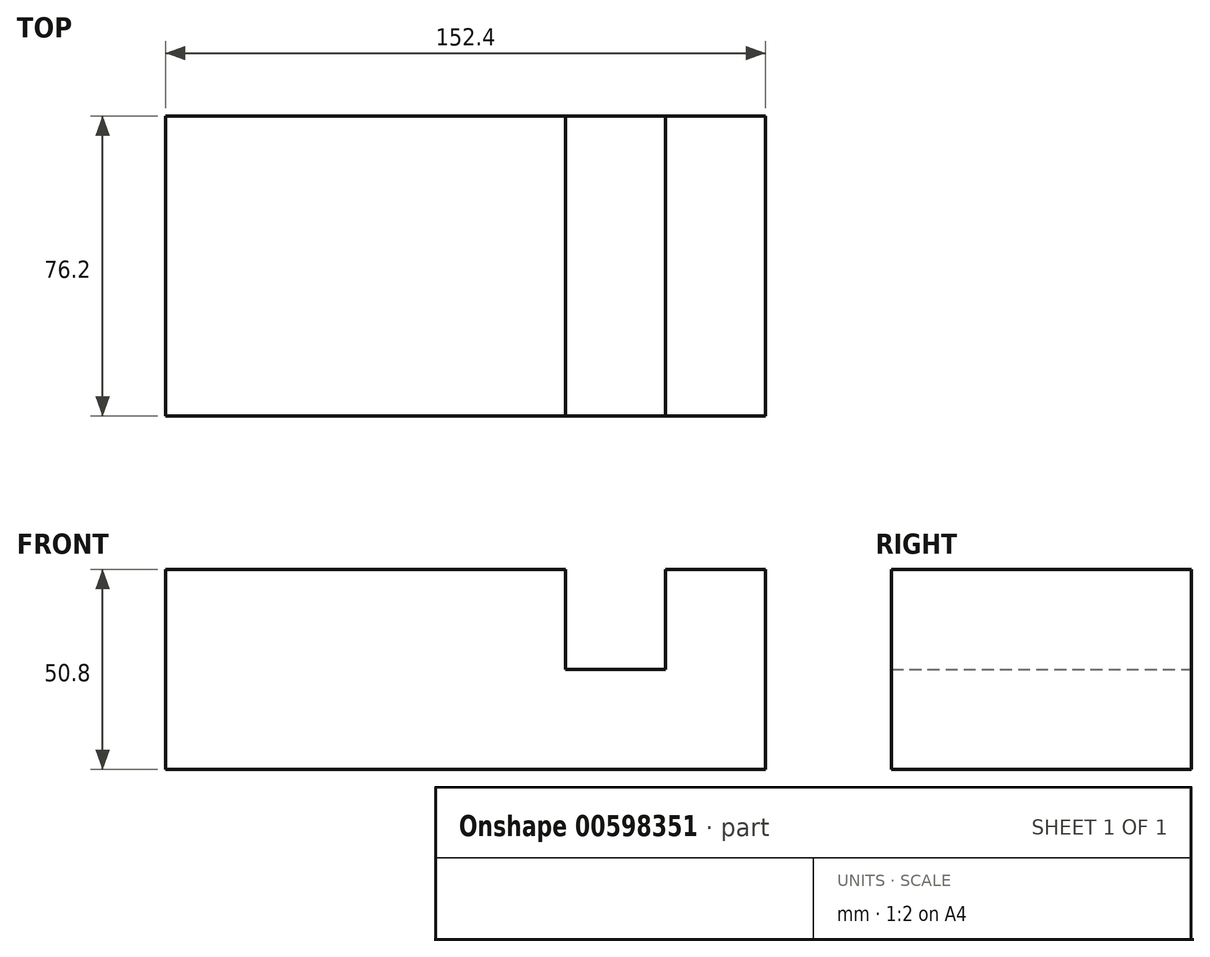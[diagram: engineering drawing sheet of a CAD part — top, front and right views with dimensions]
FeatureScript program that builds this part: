
annotation { "Feature Type Name" : "Feature", "Feature Type Description" : "" }
export const myFeature = defineFeature(function(context is Context, id is Id, definition is map)
    precondition{}
    {
        {
            var Q0;
            Q0=qCreatedBy(makeId("Front.planeOp"),FACE);
            var sketch = newSketch(context, id + "F0", { "sketchPlane" : qUnion([Q0])});
            skLineSegment(sketch, "E0", {"start": v(-49.46, 0) * mm, "end": v(102.94, 0) * mm});
            skLineSegment(sketch, "E1", {"start": v(-49.46, 0) * mm, "end": v(-49.46, 50.8) * mm});
            skLineSegment(sketch, "E2", {"start": v(102.94, 0) * mm, "end": v(102.94, 50.8) * mm});
            skLineSegment(sketch, "E3", {"start": v(102.94, 50.8) * mm, "end": v(77.54, 50.8) * mm});
            skLineSegment(sketch, "E4", {"start": v(77.54, 50.8) * mm, "end": v(77.54, 25.4) * mm});
            skLineSegment(sketch, "E5", {"start": v(77.54, 25.4) * mm, "end": v(52.14, 25.4) * mm});
            skLineSegment(sketch, "E6", {"start": v(52.14, 25.4) * mm, "end": v(52.14, 50.8) * mm});
            skLineSegment(sketch, "E7", {"start": v(52.14, 50.8) * mm, "end": v(-49.46, 50.8) * mm});
            skSolve(sketch);
        }
        {
            var Q0;
            Q0 = qSketchRegion(id + "F0", true);
            extrude(context, id + "F1", {"entities" : qUnion([Q0]), "depth" : 76.2 * mm, "offsetDistance" : 25.4 * mm});
        }
    });
